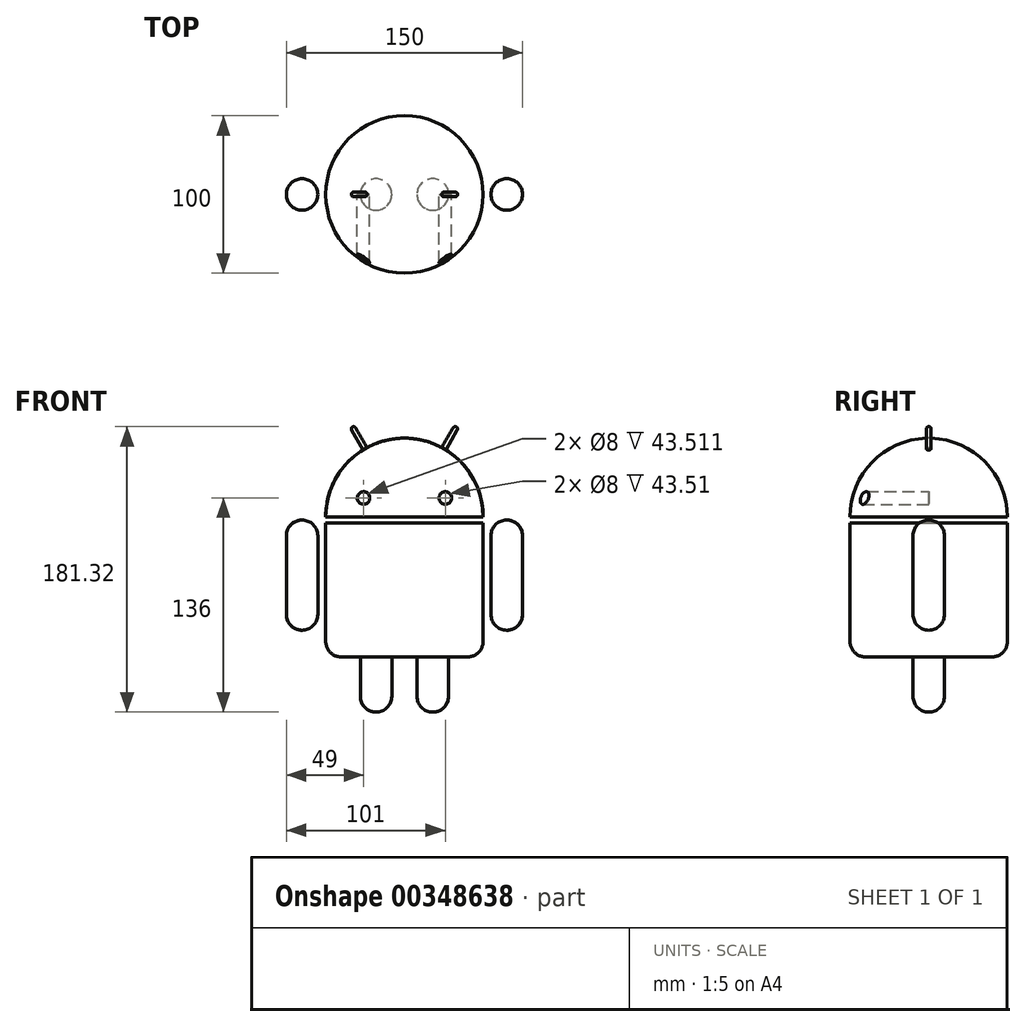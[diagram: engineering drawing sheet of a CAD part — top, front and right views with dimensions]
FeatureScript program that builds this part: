
annotation { "Feature Type Name" : "Feature", "Feature Type Description" : "" }
export const myFeature = defineFeature(function(context is Context, id is Id, definition is map)
    precondition{}
    {
        {
            var Q0;
            Q0=qCreatedBy(makeId("Front.planeOp"),FACE);
            var sketch = newSketch(context, id + "F0", { "sketchPlane" : qUnion([Q0])});
            skLineSegment(sketch, "E0", {"start": v(0, 63.5) * mm, "end": v(0, -112.89) * mm, "construction": true});
            skLineSegment(sketch, "E1", {"start": v(0, 0) * mm, "end": v(50, 0) * mm});
            skLineSegment(sketch, "E2", {"start": v(50, 0) * mm, "end": v(50, -75) * mm});
            skLineSegment(sketch, "E3", {"start": v(40, -85) * mm, "end": v(0, -85) * mm});
            skLineSegment(sketch, "E4", {"start": v(0, -85) * mm, "end": v(0, 0) * mm});
            skLineSegment(sketch, "E5", {"start": v(0, 4) * mm, "end": v(50, 4) * mm});
            skLineSegment(sketch, "E6", {"start": v(0, 4) * mm, "end": v(0, 54) * mm});
            skArc(sketch, "E7", {"start": v(50, 4) * mm, "mid": v(35.36, 39.36) * mm, "end": v(0, 54) * mm});
            skLineSegment(sketch, "E8", {"start": v(0, 54) * mm, "end": v(-42.59, 54) * mm, "construction": true});
            skPoint(sketch, "E9.visualSharp", {"position": v(50, -85) * mm});
            skArc(sketch, "E9.filletArc", {"start": v(40, -85) * mm, "mid": v(47.07, -82.07) * mm, "end": v(50, -75) * mm});
            skSolve(sketch);
        }
        {
            var Q0;
            Q0=makeQuery(id+"F0.imprint","IMPRINT",FACE,{"disambiguationData":[TD([[makeQuery(id+"F0.imprint","IMPRINT",EDGE,{"derivedFrom":sQuery(id+"F0.wireOp",EDGE,"E5")}),1.0]])]});
            var Q1;
            Q1=makeQuery(id+"F0.imprint","IMPRINT",FACE,{"disambiguationData":[TD([[makeQuery(id+"F0.imprint","IMPRINT",EDGE,{"derivedFrom":sQuery(id+"F0.wireOp",EDGE,"E1")}),-1.0]])]});
            var Q2;
            Q2=sQuery(id+"F0.wireOp",EDGE,"E0");
            revolve(context, id + "F1", {"entities" : qUnion([Q0, Q1]), "axis" : qUnion([Q2]), "revolveType" : RevolveType.FULL});
        }
        {
            var Q0;
            Q0=qCreatedBy(makeId("Front.planeOp"),FACE);
            var sketch = newSketch(context, id + "F2", { "sketchPlane" : qUnion([Q0])});
            skLineSegment(sketch, "E10", {"start": v(18, -77.06) * mm, "end": v(18, -138.1) * mm, "construction": true});
            skLineSegment(sketch, "E11", {"start": v(18, -85) * mm, "end": v(28, -85) * mm});
            skLineSegment(sketch, "E12", {"start": v(28, -85) * mm, "end": v(28, -110) * mm});
            skLineSegment(sketch, "E13", {"start": v(18, -120) * mm, "end": v(18, -120) * mm});
            skLineSegment(sketch, "E14", {"start": v(18, -120) * mm, "end": v(18, -85) * mm});
            skPoint(sketch, "E15.visualSharp", {"position": v(28, -120) * mm});
            skArc(sketch, "E15.filletArc", {"start": v(18, -120) * mm, "mid": v(25.07, -117.07) * mm, "end": v(28, -110) * mm});
            skSolve(sketch);
        }
        {
            var Q0;
            Q0=makeQuery(id+"F2.imprint","IMPRINT",FACE,{"disambiguationData":[TD([[makeQuery(id+"F2.imprint","IMPRINT",EDGE,{"derivedFrom":sQuery(id+"F2.wireOp",EDGE,"E11")}),-1.0]])]});
            var Q1;
            Q1=sQuery(id+"F2.wireOp",EDGE,"E10");
            revolve(context, id + "F3", {"operationType" : NewBodyOperationType.ADD, "entities" : qUnion([Q0]), "axis" : qUnion([Q1]), "revolveType" : RevolveType.FULL});
        }
        {
            var Q0;
            Q0=qCreatedBy(makeId("Front.planeOp"),FACE);
            var sketch = newSketch(context, id + "F4", { "sketchPlane" : qUnion([Q0])});
            skLineSegment(sketch, "E16", {"start": v(65, 12.15) * mm, "end": v(65, -85.61) * mm, "construction": true});
            skLineSegment(sketch, "E17.bottom", {"start": v(65, -68) * mm, "end": v(65, -68) * mm});
            skLineSegment(sketch, "E17.top", {"start": v(65, 2) * mm, "end": v(65, 2) * mm});
            skLineSegment(sketch, "E17.left", {"start": v(65, -68) * mm, "end": v(65, 2) * mm});
            skLineSegment(sketch, "E17.right", {"start": v(75, -58) * mm, "end": v(75, -8) * mm});
            skPoint(sketch, "E18.visualSharp", {"position": v(75, -68) * mm});
            skArc(sketch, "E18.filletArc", {"start": v(65, -68) * mm, "mid": v(72.07, -65.07) * mm, "end": v(75, -58) * mm});
            skPoint(sketch, "E19.visualSharp", {"position": v(75, 2) * mm});
            skArc(sketch, "E19.filletArc", {"start": v(75, -8) * mm, "mid": v(72.07, -0.93) * mm, "end": v(65, 2) * mm});
            skSolve(sketch);
        }
        {
            var Q0;
            Q0=qSketchRegion(id+"F4",true);
            var Q1;
            Q1=sQuery(id+"F4.wireOp",EDGE,"E16");
            revolve(context, id + "F5", {"entities" : qUnion([Q0]), "axis" : qUnion([Q1]), "revolveType" : RevolveType.FULL});
        }
        {
            var Q0;
            Q0=qCreatedBy(makeId("Front.planeOp"),FACE);
            var sketch = newSketch(context, id + "F6", { "sketchPlane" : qUnion([Q0])});
            skLineSegment(sketch, "E20", {"start": v(0, 3.96) * mm, "end": v(16.28, 32.17) * mm, "construction": true});
            skLineSegment(sketch, "E21", {"start": v(23, 43.8) * mm, "end": v(24.3, 43.05) * mm});
            skLineSegment(sketch, "E22", {"start": v(24.3, 43.05) * mm, "end": v(33.55, 59.07) * mm});
            skLineSegment(sketch, "E23", {"start": v(33, 61.12) * mm, "end": v(33, 61.12) * mm});
            skLineSegment(sketch, "E24", {"start": v(33, 61.12) * mm, "end": v(23, 43.8) * mm});
            skPoint(sketch, "E25.visualSharp", {"position": v(34.3, 60.37) * mm});
            skArc(sketch, "E25.filletArc", {"start": v(33.55, 59.07) * mm, "mid": v(33.7, 60.2) * mm, "end": v(33, 61.12) * mm});
            skSolve(sketch);
        }
        {
            var Q0;
            Q0=qSketchRegion(id+"F6",true);
            var Q1;
            Q1=sQuery(id+"F6.wireOp",EDGE,"E20");
            revolve(context, id + "F7", {"operationType" : NewBodyOperationType.ADD, "entities" : qUnion([Q0]), "axis" : qUnion([Q1]), "revolveType" : RevolveType.FULL});
        }
        {
            var Q0;
            Q0=makeQuery(id+"F5.opRevolve","SWEPT_BODY",BODY,{"disambiguationData":[OSD([sQuery(id+"F4.wireOp",EDGE,"E17.left"),sQuery(id+"F4.wireOp",EDGE,"E17.right"),sQuery(id+"F4.wireOp",EDGE,"E18.filletArc"),sQuery(id+"F4.wireOp",EDGE,"E19.filletArc")])]});
            var Q1;
            Q1=makeQuery(id+"F1.opRevolve","SWEPT_BODY",BODY,{"disambiguationData":[OSD([sQuery(id+"F0.wireOp",EDGE,"E1"),sQuery(id+"F0.wireOp",EDGE,"E2"),sQuery(id+"F0.wireOp",EDGE,"E3"),sQuery(id+"F0.wireOp",EDGE,"E4"),sQuery(id+"F0.wireOp",EDGE,"E9.filletArc")])]});
            var Q2;
            Q2=makeQuery(id+"F1.opRevolve","SWEPT_BODY",BODY,{"disambiguationData":[OSD([sQuery(id+"F0.wireOp",EDGE,"E5"),sQuery(id+"F0.wireOp",EDGE,"E6"),sQuery(id+"F0.wireOp",EDGE,"E7")])]});
            var Q3;
            Q3=qCreatedBy(makeId("Right.planeOp"),FACE);
            mirror(context, id + "F8", {"entities" : qUnion([Q0, Q1, Q2]), "mirrorPlane" : qUnion([Q3])});
        }
        {
            var Q0;
            Q0=qCreatedBy(makeId("Front.planeOp"),FACE);
            var sketch = newSketch(context, id + "F9", { "sketchPlane" : qUnion([Q0])});
            skCircle(sketch, "E26", {"center": v(26, 16) * mm, "radius": 4 * mm});
            skCircle(sketch, "E27", {"center": v(-26, 16) * mm, "radius": 4 * mm});
            skSolve(sketch);
        }
        {
            var Q0;
            Q0=qSketchRegion(id+"F9",true);
            extrude(context, id + "F10", {"entities" : qUnion([Q0]), "operationType" : NewBodyOperationType.REMOVE, "depth" : 60 * mm});
        }
    });
